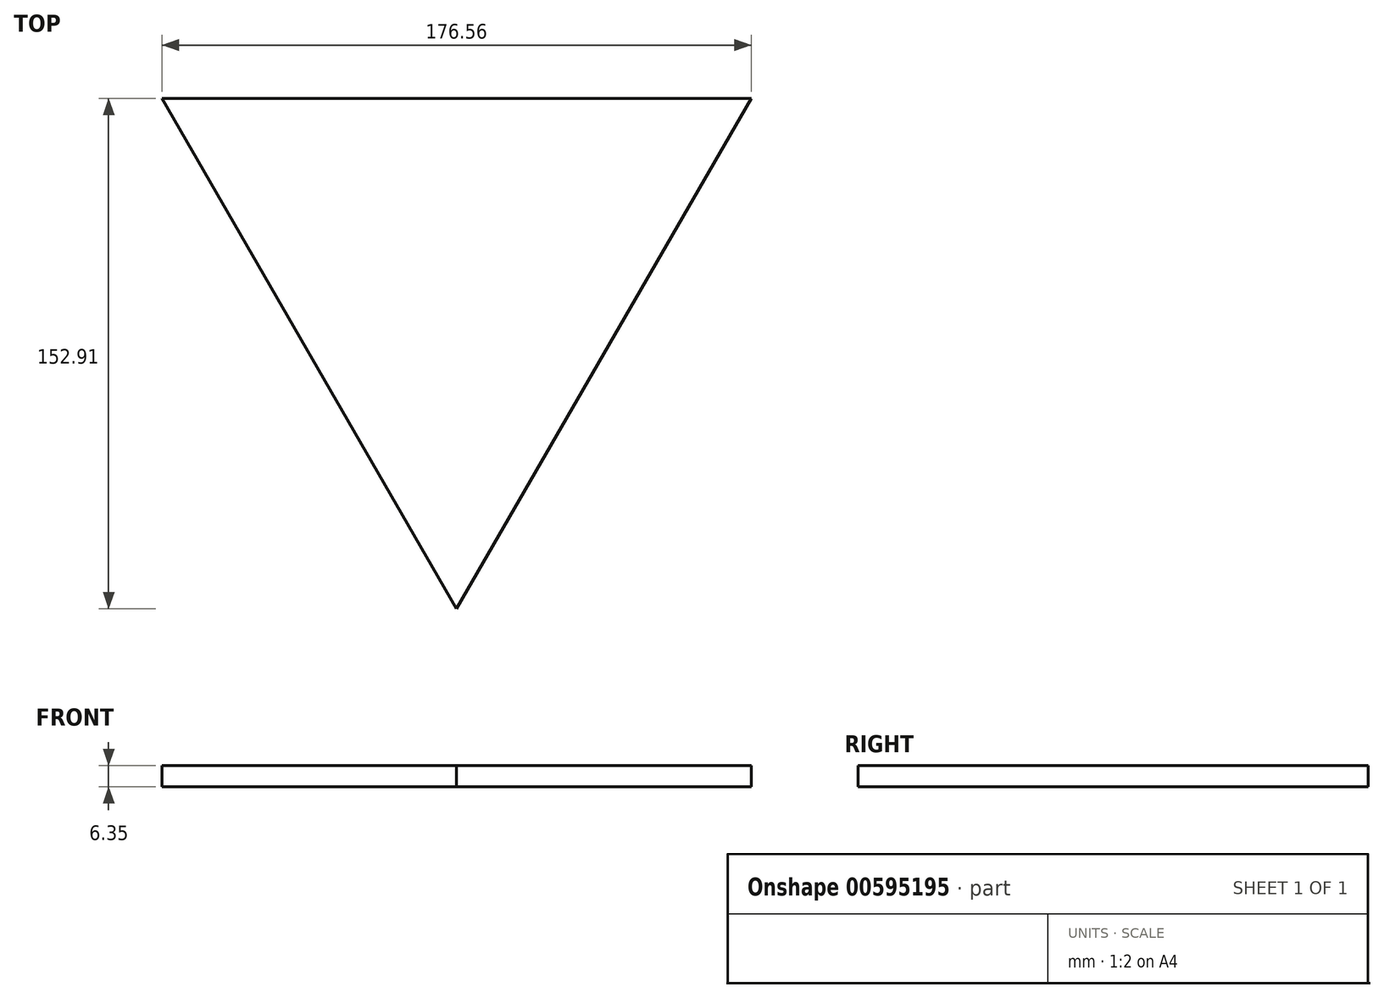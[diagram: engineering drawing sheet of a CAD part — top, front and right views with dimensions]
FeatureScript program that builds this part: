
annotation { "Feature Type Name" : "Feature", "Feature Type Description" : "" }
export const myFeature = defineFeature(function(context is Context, id is Id, definition is map)
    precondition{}
    {
        {
            var Q0;
            Q0=qCreatedBy(makeId("Top.planeOp"),FACE);
            var sketch = newSketch(context, id + "F0", { "sketchPlane" : qUnion([Q0])});
            skCircle(sketch, "E0.cCircle", {"center": v(0, -23.05) * mm, "radius": 50.97 * mm, "construction": true});
            skLineSegment(sketch, "E0.0", {"start": v(-88.28, 27.92) * mm, "end": v(88.28, 27.92) * mm});
            skLineSegment(sketch, "E0.1", {"start": v(88.28, 27.92) * mm, "end": v(0, -125) * mm});
            skLineSegment(sketch, "E0.2", {"start": v(0, -125) * mm, "end": v(-88.28, 27.92) * mm});
            skPoint(sketch, "E0.0.midPoint", {"position": v(0, 27.92) * mm});
            skSolve(sketch);
        }
        {
            var Q0;
            {var subQ0=sQuery(id+"F0.wireOp",EDGE,"E0.0");Q0=makeQuery(id+"F0.imprint","IMPRINT",FACE,{"disambiguationData":[TD([[makeQuery(id+"F0.imprint","IMPRINT",EDGE,{"derivedFrom":subQ0}),-1.0]])]});}
            extrude(context, id + "F1", {"entities" : qUnion([Q0]), "depth" : 6.35 * mm, "offsetDistance" : 25.4 * mm});
        }
        {
            var Q0;
            Q0 = qSketchRegion(id + "F0", true);
            extrude(context, id + "F2", {"entities" : qUnion([Q0]), "operationType" : NewBodyOperationType.ADD, "depth" : 6.35 * mm, "offsetDistance" : 25.4 * mm});
        }
    });
